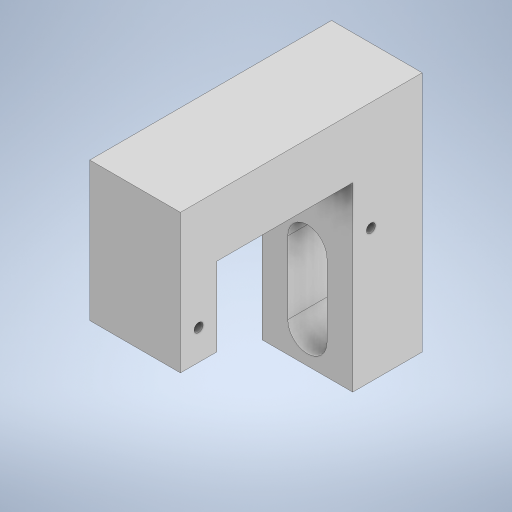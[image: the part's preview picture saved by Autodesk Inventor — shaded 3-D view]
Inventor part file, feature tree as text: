
AUTODESK INVENTOR PART (.ipt)
format: ipt  version: 2023 (Build 270158000, 158)  size: 228,352 bytes
history: native  units: mm
features: extrude x2, sketch x2
ambient origin geometry x8: Origin, YZ Plane, XZ Plane, XY Plane, X Axis, Y Axis, Z Axis, Center Point
bodies: Solid1 (feature_tree)
feature tree (4):
  extrude  "Extrusion1"  Depth=13.0mm
  extrude  "Extrusion2"  Depth=22.5mm
  sketch  "Sketch1"  dims[d0=40.0mm d1=13.0mm]
  sketch  "Sketch3"  dims[d2=6.0mm d3=22.5mm d4=1.5mm d5=5.0mm d7=10.0mm d9=30.0mm d10=1.5mm d11=3.0mm d12=15.0mm d13=0.0mm d14=6.5mm d15=12.0mm d16=0.0mm d17=0.0mm]
